# Revit family: LFll-TY3934_Imperial
name_source: partatom
category: Sprinklers
units: mm (PartAtom-declared; Revit-internal decimal feet)

## family parameters
Always vertical = Yes
Cut with Voids When Loaded = No
Maintain Annotation Orientation = No
OmniClass Number = 23.65.70.17.11.24
OmniClass Title = Fire Fighting Sprinkler Heads
Part Type = Normal
Room Calculation Point = No
Round Connector Dimension = Use Diameter
Shared = No
Work Plane-Based = No

## types (10) — shared parameters
COBie = Yes
COBie.Component.Name = Sprinklers:Pendent
COBie.Type = Yes
COBie.Type.AssetType = Fixed
COBie.Type.Category = Pr_70_55_97_84:Sprinklers
COBie.Type.DurationUnit = year
COBie.Type.Manufacturer = Tyco Fire Protection Products
COBie.Type.Material = Brass
COBie.Type.NominalHeight = 0' - 0"
COBie.Type.NominalLength = 0' - 0"
COBie.Type.NominalWidth = 0' - 0"
COBie.Type.Shape = Cylinder
COBie.Type.Size = 1/2"(DN15)
COBie.Type.WarrantyGuarantorParts = http://tycofsbp.com
Coverage = Standard
Coverage_ = Standard
Default Elevation = 0' - 0"
K-Factor = 5.799
Manufacturer = Tyco Fire Protection Products
Manufacturer URL = www.tyco-fire.com
Material_ = Brass
Model = LFII
Nominal Diameter 1 = 1"
Orifice = Extra Large
Orifice Size = 0"
Outside Diameter 1 = 1"
Response = Quick
Response_ = Quick
SIN No = TY3934
Takeout 1 = 2"
Technical Data Sheet No = TFP401
zero-valued in all types: COBie.Type.ReplacementCost, Style Id

## per-type parameters (varying)
| type | COBie.Component.Description | COBie.Type.Colour | COBie.Type.Finish | COBie.Type.ModelNumber | COBie.Type.ModelReference | Description | Finish_ | Part No | Temperature Rating |
| LF II Pendent, Fast Response Brass 68°C/155°F 1/2" NPT_51-058-1-155 | LFII Pendent Residential FR 155°F K5.8 1/2 NPT | Yellow | Natural Brass | 51-058-1-155 | LFII Pendent Residential FR 155°F K5.8 1/2 NPT | LFII Pendent Residential FR 155°F K5.8 1/2 NPT | Natural Brass | 51-058-1-155 | 155 °F |
| LF II Pendent, Fast Response Brass 79°C/175°F 1/2" NPT_51-058-1-175 | LFII Pendent Residential FR 175°F K5.8 1/2 NPT | Yellow | Natural Brass | 51-058-1-175 | LFII Pendent Residential FR 175°F K5.8 1/2 NPT | LFII Pendent Residential FR 175°F K5.8 1/2 NPT | Natural Brass | 51-058-1-175 | 175 °F |
| LF II Pendent, Fast Response White 68°C/155°F 1/2" NPT_51-058-3-155 | LFII Pendent Residential FR 155°F K5.8 1/2 NPT | Pure White | Brass | 51-058-3-155 | LFII Pendent Residential FR 155°F K5.8 1/2 NPT | LFII Pendent Residential FR 155°F K5.8 1/2 NPT | Pure White | 51-058-3-155 | 155 °F |
| LF II Pendent, Fast Response White 79°C/175°F 1/2" NPT_51-058-3-175 | LFII Pendent Residential FR 175°F K5.8 1/2 NPT | Pure White | Brass | 51-058-3-175 | LFII Pendent Residential FR 175°F K5.8 1/2 NPT | LFII Pendent Residential FR 175°F K5.8 1/2 NPT | Pure White | 51-058-3-175 | 175 °F |
| LF II Pendent, Fast Response White 68°C/155°F 1/2" NPT_51-058-4-155 | LFII Pendent Residential FR 155°F K5.8 1/2 NPT | Signal White | Brass | 51-058-4-155 | LFII Pendent Residential FR 155°F K5.8 1/2 NPT | LFII Pendent Residential FR 155°F K5.8 1/2 NPT | Signal White | 51-058-4-155 | 155 °F |
| LF II Pendent, Fast Response White 79°C/175°F 1/2" NPT_51-058-4-175 | LFII Pendent Residential FR 175°F K5.8 1/2 NPT | Signal White | Brass | 51-058-4-175 | LFII Pendent Residential FR 175°F K5.8 1/2 NPT | LFII Pendent Residential FR 175°F K5.8 1/2 NPT | Signal White | 51-058-4-175 | 175 °F |
| LF II Pendent, Fast Response Jet Black 68°C/155°F 1/2" NPT_51-058-5-155 | LFII Pendent Residential FR 155°F K5.8 1/2 NPT | Jet Black | Brass | 51-058-5-155 | LFII Pendent Residential FR 155°F K5.8 1/2 NPT | LFII Pendent Residential FR 155°F K5.8 1/2 NPT | Jet Black | 51-058-5-155 | 155 °F |
| LF II Pendent, Fast Response Jet Black 79°C/175°F 1/2" NPT_51-058-5-175 | LFII Pendent Residential FR 175°F K5.8 1/2 NPT | Jet Black | Brass | 51-058-5-175 | LFII Pendent Residential FR 175°F K5.8 1/2 NPT | LFII Pendent Residential FR 175°F K5.8 1/2 NPT | Jet Black | 51-058-5-175 | 175 °F |
| LF II Pendent, Fast Response Chrome 68°C/155°F 1/2" NPT_51-058-9-155 | LFII Pendent Residential FR 155°F K5.8 1/2 NPT | Chrome Plated | Brass | 51-058-9-155 | LFII Pendent Residential FR 155°F K5.8 1/2 NPT | LFII Pendent Residential FR 155°F K5.8 1/2 NPT | Chrome Plated | 51-058-9-155 | 155 °F |
| LF II Pendent, Fast Response Chrome 79°C/175°F 1/2" NPT_51-058-9-175 | LFII Pendent Residential FR 175°F K5.8 1/2 NPT | Chrome Plated | Brass | 51-058-9-175 | LFII Pendent Residential FR 175°F K5.8 1/2 NPT | LFII Pendent Residential FR 175°F K5.8 1/2 NPT | Chrome Plated | 51-058-9-175 | 175 °F |

## geometry (parser evidence)
native form markers: Blend x2, Sweep x47
no freeform markers — native parametric forms only
